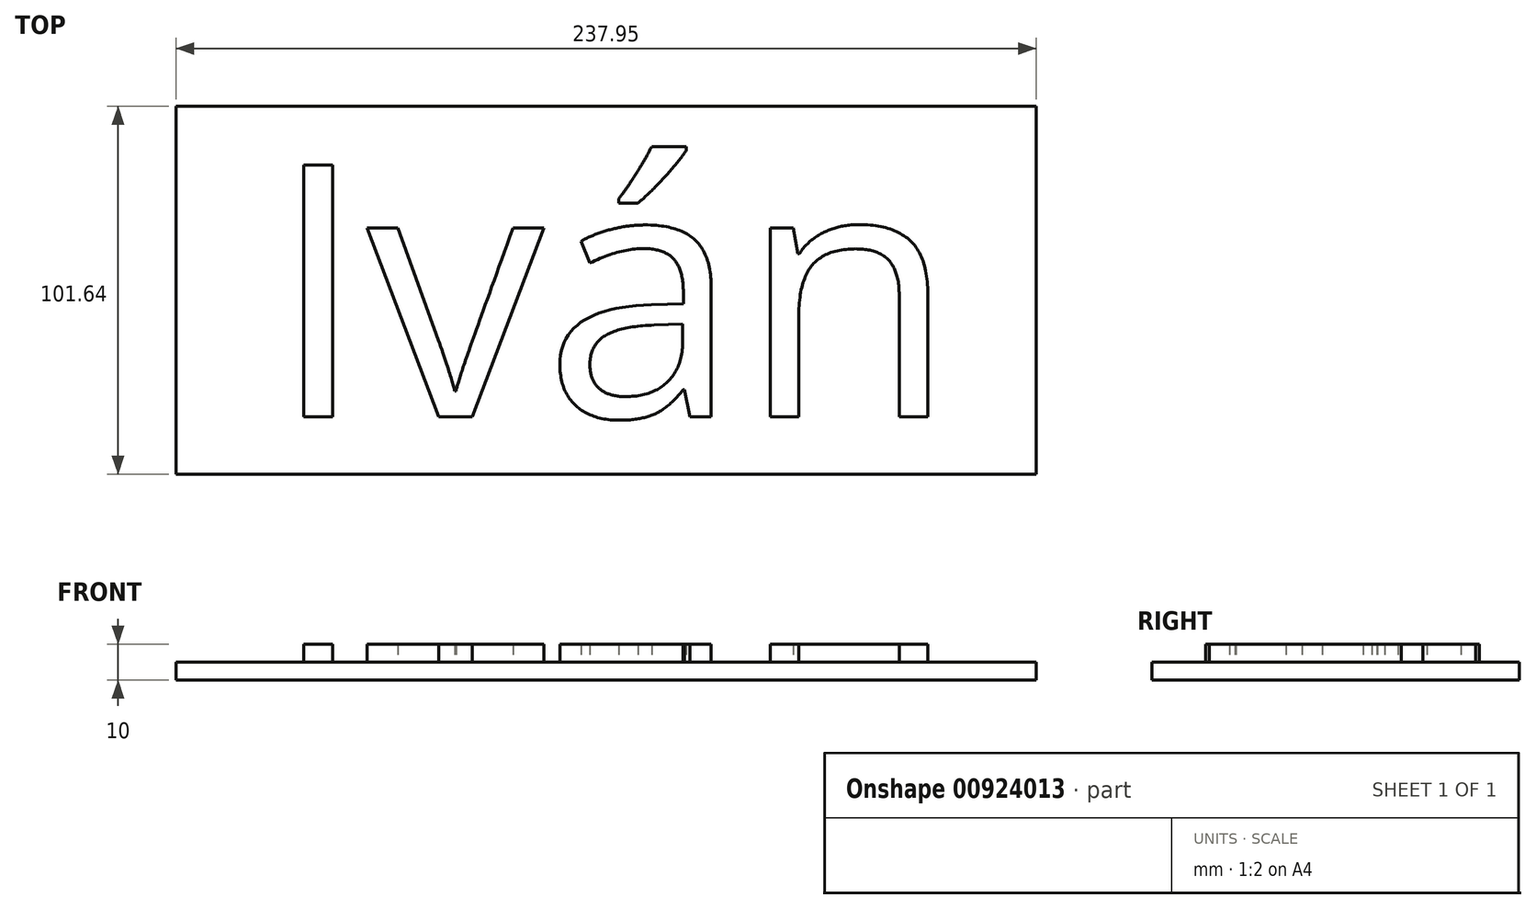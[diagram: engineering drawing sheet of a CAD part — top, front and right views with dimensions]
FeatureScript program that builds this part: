
annotation { "Feature Type Name" : "Feature", "Feature Type Description" : "" }
export const myFeature = defineFeature(function(context is Context, id is Id, definition is map)
    precondition{}
    {
        {
            var Q0;
            Q0=qCreatedBy(makeId("Top.planeOp"),FACE);
            var sketch = newSketch(context, id + "F0", { "sketchPlane" : qUnion([Q0])});
            skLineSegment(sketch, "E0.bottom", {"start": v(-116.44, 50.78) * mm, "end": v(121.51, 50.78) * mm});
            skLineSegment(sketch, "E0.top", {"start": v(-116.44, -50.86) * mm, "end": v(121.51, -50.86) * mm});
            skLineSegment(sketch, "E0.left", {"start": v(-116.44, 50.78) * mm, "end": v(-116.44, -50.86) * mm});
            skLineSegment(sketch, "E0.right", {"start": v(121.51, 50.78) * mm, "end": v(121.51, -50.86) * mm});
            skSolve(sketch);
        }
        {
            var Q0;
            Q0=makeQuery(id+"F0.imprint","IMPRINT",FACE,{"disambiguationData":[TD([[makeQuery(id+"F0.imprint","IMPRINT",EDGE,{"derivedFrom":sQuery(id+"F0.wireOp",EDGE,"E0.bottom")}),-1.0]])]});
            extrude(context, id + "F1", {"entities" : qUnion([Q0]), "depth" : 5 * mm, "offsetDistance" : 25.4 * mm});
        }
        {
            var Q0;
            Q0=makeQuery(id+"F1.opExtrude","CAP_FACE",FACE,{"disambiguationData":[OSD([sQuery(id+"F0.wireOp",EDGE,"E0.bottom"),sQuery(id+"F0.wireOp",EDGE,"E0.top"),sQuery(id+"F0.wireOp",EDGE,"E0.left"),sQuery(id+"F0.wireOp",EDGE,"E0.right")])],"isStart":false});
            shell(context, id + "F2", {"entities" : qUnion([Q0]), "thickness" : 5 * mm});
        }
        {
            var Q0;
            Q0=makeQuery(id+"F1.opExtrude","CAP_FACE",FACE,{"disambiguationData":[OSD([sQuery(id+"F0.wireOp",EDGE,"E0.bottom"),sQuery(id+"F0.wireOp",EDGE,"E0.top"),sQuery(id+"F0.wireOp",EDGE,"E0.left"),sQuery(id+"F0.wireOp",EDGE,"E0.right")])],"isStart":false});
            var sketch = newSketch(context, id + "F3", { "sketchPlane" : qUnion([Q0])});
            skText(sketch, "E1", { "text": "Iván", "fontName": "OpenSans-Regular.ttf"});
            const initialGuessF3  = {"E1": [-0.0907, -0.03502, 1, 0, 0.07019]};
            skSetInitialGuess(sketch, initialGuessF3);
            skSolve(sketch);
        }
        {
            var Q0;
            Q0 = qSketchRegion(id + "F3", true);
            extrude(context, id + "F4", {"entities" : qUnion([Q0]), "operationType" : NewBodyOperationType.ADD, "depth" : 5 * mm, "offsetDistance" : 25.4 * mm});
        }
    });
